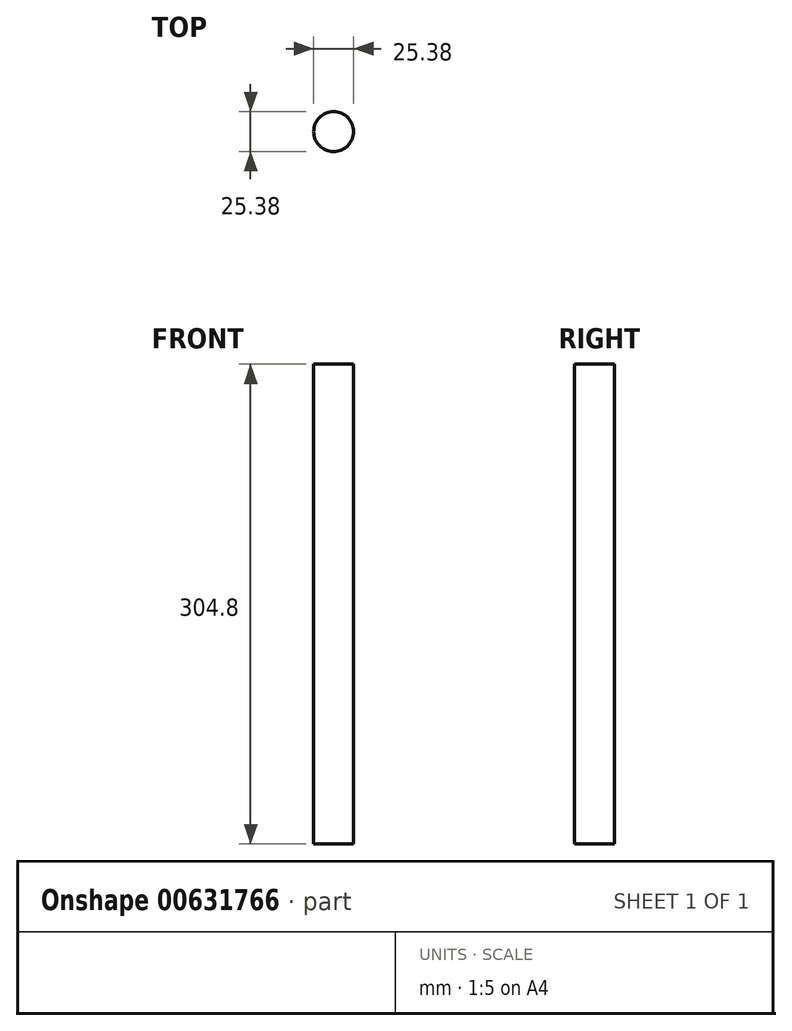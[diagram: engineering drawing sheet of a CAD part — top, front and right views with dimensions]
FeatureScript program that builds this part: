
annotation { "Feature Type Name" : "Feature", "Feature Type Description" : "" }
export const myFeature = defineFeature(function(context is Context, id is Id, definition is map)
    precondition{}
    {
        {
            var Q0;
            Q0=qCreatedBy(makeId("Top.planeOp"),FACE);
            var sketch = newSketch(context, id + "F0", { "sketchPlane" : qUnion([Q0])});
            skCircle(sketch, "E0", {"center": v(0, 0) * mm, "radius": 12.69 * mm});
            skSolve(sketch);
        }
        {
            var Q0;
            Q0=makeQuery(id+"F0.imprint","IMPRINT",FACE,{"disambiguationData":[TD([[makeQuery(id+"F0.imprint","IMPRINT",EDGE,{"derivedFrom":sQuery(id+"F0.wireOp",EDGE,"E0")}),1.0]])]});
            extrude(context, id + "F1", {"entities" : qUnion([Q0]), "endBound" : BoundingType.SYMMETRIC, "oppositeDirection" : true, "depth" : 304.8 * mm, "offsetDistance" : 25.4 * mm});
        }
    });
